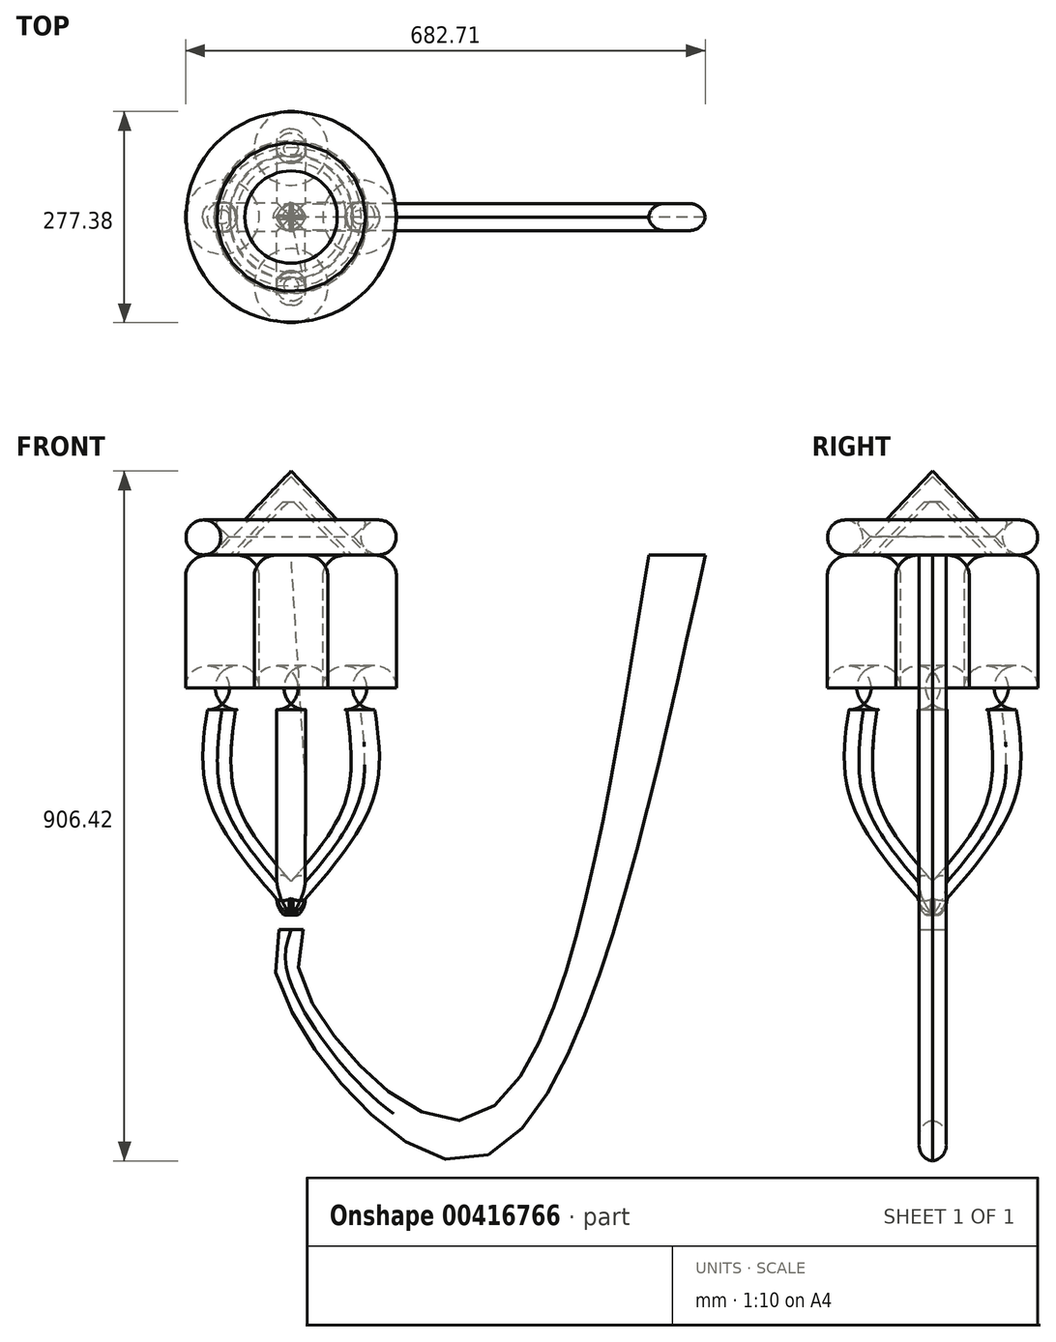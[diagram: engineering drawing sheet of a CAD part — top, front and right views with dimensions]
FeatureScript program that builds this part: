
annotation { "Feature Type Name" : "Feature", "Feature Type Description" : "" }
export const myFeature = defineFeature(function(context is Context, id is Id, definition is map)
    precondition{}
    {
        {
            var Q0;
            Q0=qCreatedBy(makeId("Front.planeOp"),FACE);
            var sketch = newSketch(context, id + "F0", { "sketchPlane" : qUnion([Q0])});
            skLineSegment(sketch, "E0", {"start": v(0, 0) * mm, "end": v(0, 77.06) * mm});
            skSolve(sketch);
        }
        {
            var Q0;
            Q0=qCreatedBy(makeId("Front.planeOp"),FACE);
            var sketch = newSketch(context, id + "F1", { "sketchPlane" : qUnion([Q0])});
            skLineSegment(sketch, "E1", {"start": v(72.14, 0) * mm, "end": v(3.54, 70.03) * mm});
            skLineSegment(sketch, "E2", {"start": v(3.54, 70.03) * mm, "end": v(10.77, 70.03) * mm});
            skLineSegment(sketch, "E3", {"start": v(10.77, 70.03) * mm, "end": v(80.41, 0) * mm});
            skLineSegment(sketch, "E4", {"start": v(80.41, 0) * mm, "end": v(80.41, 0) * mm});
            skLineSegment(sketch, "E5", {"start": v(72.14, 0) * mm, "end": v(80.41, 0) * mm});
            skLineSegment(sketch, "E6", {"start": v(100.64, 0) * mm, "end": v(0, 102.92) * mm});
            skLineSegment(sketch, "E7", {"start": v(0, 102.92) * mm, "end": v(0, 110.55) * mm});
            skLineSegment(sketch, "E8", {"start": v(0, 110.55) * mm, "end": v(105.23, 0) * mm});
            skLineSegment(sketch, "E9", {"start": v(105.23, 0) * mm, "end": v(100.64, 0) * mm});
            skLineSegment(sketch, "E10", {"start": v(81.86, 24.55) * mm, "end": v(105.23, 46.8) * mm});
            skLineSegment(sketch, "E11", {"start": v(105.23, 46.8) * mm, "end": v(60.68, 46.8) * mm});
            skSolve(sketch);
        }
        {
            var Q0;
            Q0=makeQuery(id+"F1.imprint","IMPRINT",FACE,{"disambiguationData":[TD([[makeQuery(id+"F1.imprint","IMPRINT",EDGE,{"derivedFrom":sQuery(id+"F1.wireOp",EDGE,"E6")}),-1.0]])]});
            var Q1;
            Q1=makeQuery(id+"F1.imprint","IMPRINT",FACE,{"disambiguationData":[TD([[makeQuery(id+"F1.imprint","IMPRINT",EDGE,{"derivedFrom":sQuery(id+"F1.wireOp",EDGE,"E1")}),-1.0]])]});
            var Q2;
            Q2=sQuery(id+"F0.wireOp",EDGE,"E0");
            revolve(context, id + "F2", {"entities" : qUnion([Q0, Q1]), "axis" : qUnion([Q2]), "revolveType" : RevolveType.FULL});
        }
        {
            var Q0;
            Q0=qCreatedBy(makeId("Top.planeOp"),FACE);
            var sketch = newSketch(context, id + "F3", { "sketchPlane" : qUnion([Q0])});
            skCircle(sketch, "E12", {"center": v(0, -90.17) * mm, "radius": 48.52 * mm});
            skSolve(sketch);
        }
        {
            var Q0;
            Q0=makeQuery(id+"F3.imprint","IMPRINT",FACE,{"disambiguationData":[TD([[makeQuery(id+"F3.imprint","IMPRINT",EDGE,{"derivedFrom":sQuery(id+"F3.wireOp",EDGE,"E12")}),1.0]])]});
            extrude(context, id + "F4", {"entities" : qUnion([Q0]), "oppositeDirection" : true, "depth" : 203.2 * mm});
        }
        {
            var Q0;
            Q0=makeQuery(id+"F4.opExtrude","CAP_FACE",FACE,{"disambiguationData":[OSD([sQuery(id+"F3.wireOp",EDGE,"E12")])],"isStart":false});
            var Q1;
            Q1=makeQuery(id+"F4.opExtrude","CAP_EDGE",EDGE,{"disambiguationData":[OSD([sQuery(id+"F3.wireOp",EDGE,"E12")])],"isStart":true});
            fillet(context, id + "F5", {"entities" : qUnion([Q0, Q1]), "radius" : 28.95 * mm, "tangentPropagation" : true, "allowEdgeOverflow" : false});
        }
        {
            var Q0;
            Q0=makeQuery(id+"F4.opExtrude","SWEPT_BODY",BODY,{"disambiguationData":[OSD([sQuery(id+"F3.wireOp",EDGE,"E12")])]});
            var Q1;
            Q1=sQuery(id+"F0.wireOp",EDGE,"E0");
            circularPattern(context, id + "F6", {"entities" : qUnion([Q0]), "axis" : qUnion([Q1]), "angle" : 360 * degree, "instanceCount" : 4, "equalSpace" : true, "computeTransformsWithoutBuiltin" : true});
        }
        {
            var Q0;
            Q0=makeQuery(id+"F2.opRevolve","SWEPT_EDGE",EDGE,{"disambiguationData":[OSD([sQuery(id+"F1.wireOp",EDGE,"E8"),sQuery(id+"F1.wireOp",EDGE,"E9")])]});
            chamfer(context, id + "F7", {"entities" : qUnion([Q0]), "width" : 5.08 * mm, "tangentPropagation" : true});
        }
        {
            var Q0;
            {var subQ0=sQuery(id+"F1.wireOp",EDGE,"E8");Q0=makeQuery(id+"F7.opChamfer","BLEND_EDGE",EDGE,{"blendedFrom":[makeQuery(id+"F2.opRevolve","SWEPT_EDGE",EDGE,{"disambiguationData":[OSD([subQ0,sQuery(id+"F1.wireOp",EDGE,"E9")])]}),makeQuery(id+"F2.opRevolve","SWEPT_FACE",FACE,{"disambiguationData":[OSD([subQ0])]})],"blendedInto":[makeQuery(id+"F2.opRevolve","SWEPT_FACE",FACE,{"disambiguationData":[OSD([subQ0])]})]});}
            fillet(context, id + "F8", {"entities" : qUnion([Q0]), "radius" : 5.08 * mm, "tangentPropagation" : true, "allowEdgeOverflow" : false});
        }
        {
            var Q0;
            {var subQ0=sQuery(id+"F1.wireOp",EDGE,"E10");Q0=makeQuery(id+"F1.imprint","IMPRINT",FACE,{"disambiguationData":[TD([[makeQuery(id+"F1.imprint","IMPRINT",EDGE,{"derivedFrom":subQ0}),1.0]])]});}
            var Q1;
            Q1=sQuery(id+"F0.wireOp",EDGE,"E0");
            revolve(context, id + "F9", {"operationType" : NewBodyOperationType.ADD, "entities" : qUnion([Q0]), "axis" : qUnion([Q1]), "revolveType" : RevolveType.FULL});
        }
        {
            var Q0;
            Q0=makeQuery(id+"F9.opRevolve","SWEPT_EDGE",EDGE,{"disambiguationData":[OSD([sQuery(id+"F1.wireOp",EDGE,"E10"),sQuery(id+"F1.wireOp",EDGE,"E11")])]});
            fillet(context, id + "F10", {"entities" : qUnion([Q0]), "radius" : 5.08 * mm, "tangentPropagation" : true, "allowEdgeOverflow" : false});
        }
        {
            var Q0;
            Q0=qCreatedBy(makeId("Front.planeOp"),FACE);
            var sketch = newSketch(context, id + "F11", { "sketchPlane" : qUnion([Q0])});
            skCircle(sketch, "E13", {"center": v(115.11, 23.34) * mm, "radius": 22.9 * mm});
            skPoint(sketch, "E13.first.point", {"position": v(96.33, 36.45) * mm});
            skPoint(sketch, "E13.second.point", {"position": v(134.49, 11.11) * mm});
            skPoint(sketch, "E13.third.point", {"position": v(137.99, 24.6) * mm});
            skSolve(sketch);
        }
        {
            var Q0;
            Q0 = qSketchRegion(id + "F11", true);
            var Q1;
            Q1=sQuery(id+"F0.wireOp",EDGE,"E0");
            revolve(context, id + "F12", {"entities" : qUnion([Q0]), "axis" : qUnion([Q1]), "revolveType" : RevolveType.FULL});
        }
        {
            var Q0;
            Q0=qCreatedBy(makeId("Front.planeOp"),FACE);
            var sketch = newSketch(context, id + "F13", { "sketchPlane" : qUnion([Q0])});
            skFitSpline(sketch, "E14", {"points": [v(108.96, -196.19) * mm, v(108.16, -318.96) * mm, v(0, -472.67) * mm], "startDerivative": vector(41.53, -273.95) * mm, "endDerivative": vector(-249.18, -278.84) * mm});
            skLineSegment(sketch, "E15", {"start": v(108.96, -196.19) * mm, "end": v(72.2, -196.19) * mm});
            skLineSegment(sketch, "E16", {"start": v(-2.54, -472.56) * mm, "end": v(-2.54, -431.58) * mm});
            skFitSpline(sketch, "E17", {"points": [v(72.2, -196.19) * mm, v(72.2, -320.95) * mm, v(-2.54, -431.58) * mm], "startDerivative": vector(36.12, -262.74) * mm, "endDerivative": vector(-184.34, -208.36) * mm});
            skLineSegment(sketch, "E18", {"start": v(-2.54, -472.56) * mm, "end": v(0, -472.67) * mm});
            skSolve(sketch);
        }
        {
            var Q0;
            Q0=makeQuery(id+"F13.imprint","IMPRINT",FACE,{"disambiguationData":[TD([[makeQuery(id+"F13.imprint","IMPRINT",EDGE,{"derivedFrom":sQuery(id+"F13.wireOp",EDGE,"E14")}),-1.0]])]});
            extrude(context, id + "F14", {"entities" : qUnion([Q0]), "operationType" : NewBodyOperationType.ADD, "depth" : 38.1 * mm, "symmetric" : true});
        }
        {
            var Q0;
            Q0=makeQuery(id+"F14.opExtrude","CAP_EDGE",EDGE,{"disambiguationData":[OSD([sQuery(id+"F13.wireOp",EDGE,"E14")])],"isStart":false});
            var Q1;
            Q1=makeQuery(id+"F14.opExtrude","CAP_EDGE",EDGE,{"disambiguationData":[OSD([sQuery(id+"F13.wireOp",EDGE,"E14")])],"isStart":true});
            var Q2;
            Q2=makeQuery(id+"F14.opExtrude","CAP_EDGE",EDGE,{"disambiguationData":[OSD([sQuery(id+"F13.wireOp",EDGE,"E17")])],"isStart":false});
            var Q3;
            Q3=makeQuery(id+"F14.opExtrude","CAP_EDGE",EDGE,{"disambiguationData":[OSD([sQuery(id+"F13.wireOp",EDGE,"E17")])],"isStart":true});
            fillet(context, id + "F15", {"entities" : qUnion([Q0, Q1, Q2, Q3]), "radius" : 17.78 * mm, "tangentPropagation" : true, "allowEdgeOverflow" : false});
        }
        {
            var Q0;
            Q0=makeQuery(id+"F6.opPattern","COPY",BODY,{"derivedFrom":makeQuery(id+"F4.opExtrude","SWEPT_BODY",BODY,{"disambiguationData":[OSD([sQuery(id+"F3.wireOp",EDGE,"E12")])]}),"instanceName":"1"});
            var Q1;
            Q1=sQuery(id+"F0.wireOp",EDGE,"E0");
            circularPattern(context, id + "F16", {"operationType" : NewBodyOperationType.ADD, "entities" : qUnion([Q0]), "axis" : qUnion([Q1]), "angle" : 360 * degree, "instanceCount" : 4, "equalSpace" : true, "computeTransformsWithoutBuiltin" : true});
        }
        {
            var Q0;
            {var subQ0=makeQuery(id+"F14.opExtrude","SWEPT_FACE",FACE,{"disambiguationData":[OSD([sQuery(id+"F13.wireOp",EDGE,"E18")])]});var subQ1=subQ0;var subQ3=makeQuery(id+"F14.opExtrude","SWEPT_FACE",FACE,{"disambiguationData":[OSD([sQuery(id+"F13.wireOp",EDGE,"E16")])]});var subQ4=makeQuery(id+"F16.opPattern","COPY",FACE,{"derivedFrom":subQ1,"instanceName":"3"});Q0=makeQuery(id+"F16.boolean.opBoolean","SPLIT",FACE,{"disambiguationData":[TD([subQ3])],"derivedFrom":subQ4});}
            var sketch = newSketch(context, id + "F17", { "sketchPlane" : qUnion([Q0])});
            skCircle(sketch, "E19", {"center": v(0, 20.35) * mm, "radius": 16.3 * mm});
            skSolve(sketch);
        }
        {
            var Q0;
            Q0=sQuery(id+"F17.wireOp",EDGE,"E19");
            extrude(context, id + "F18", {"bodyType" : ExtendedToolBodyType.SURFACE, "surfaceEntities" : qUnion([Q0]), "depth" : 38.1 * mm, "symmetric" : true});
        }
        {
            var Q0;
            Q0=qCreatedBy(makeId("Front.planeOp"),FACE);
            var sketch = newSketch(context, id + "F19", { "sketchPlane" : qUnion([Q0])});
            skLineSegment(sketch, "E20", {"start": v(-15.91, -491.7) * mm, "end": v(16.12, -491.7) * mm});
            skLineSegment(sketch, "E21", {"start": v(469.53, 0) * mm, "end": v(544.19, 0) * mm});
            skFitSpline(sketch, "E22", {"points": [v(16.12, -491.7) * mm, v(16.12, -564.09) * mm, v(221.92, -742.55) * mm, v(469.53, 0) * mm], "startDerivative": vector(-126.15, -362.2) * mm, "endDerivative": vector(331.7, 2082.98) * mm});
            skFitSpline(sketch, "E23", {"points": [v(-15.91, -491.7) * mm, v(-15.91, -564.09) * mm, v(221.92, -796.03) * mm, v(544.19, 0) * mm], "startDerivative": vector(-128.25, -363.6) * mm, "endDerivative": vector(496.11, 2286.08) * mm});
            skSolve(sketch);
        }
        {
            var Q0;
            Q0 = qSketchRegion(id + "F19", true);
            extrude(context, id + "F20", {"entities" : qUnion([Q0]), "depth" : 35.56 * mm, "symmetric" : true});
        }
        {
            var Q0;
            Q0=makeQuery(id+"F20.opExtrude","CAP_EDGE",EDGE,{"disambiguationData":[OSD([sQuery(id+"F19.wireOp",EDGE,"E23")])],"isStart":false});
            var Q1;
            Q1=makeQuery(id+"F20.opExtrude","CAP_EDGE",EDGE,{"disambiguationData":[OSD([sQuery(id+"F19.wireOp",EDGE,"E22")])],"isStart":true});
            var Q2;
            Q2=makeQuery(id+"F20.opExtrude","CAP_EDGE",EDGE,{"disambiguationData":[OSD([sQuery(id+"F19.wireOp",EDGE,"E23")])],"isStart":true});
            var Q3;
            Q3=makeQuery(id+"F20.opExtrude","CAP_EDGE",EDGE,{"disambiguationData":[OSD([sQuery(id+"F19.wireOp",EDGE,"E22")])],"isStart":false});
            fillet(context, id + "F21", {"entities" : qUnion([Q0, Q1, Q2, Q3]), "radius" : 20.32 * mm, "tangentPropagation" : true, "allowEdgeOverflow" : false});
        }
    });
